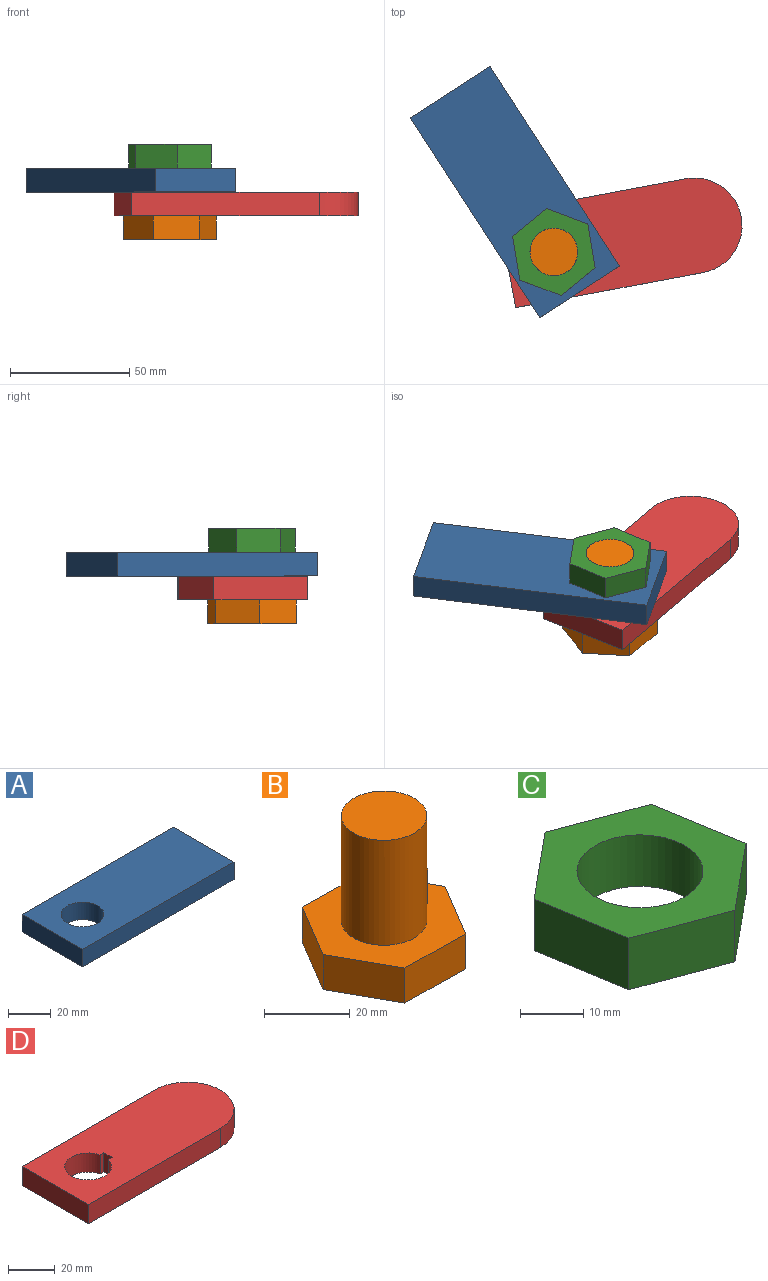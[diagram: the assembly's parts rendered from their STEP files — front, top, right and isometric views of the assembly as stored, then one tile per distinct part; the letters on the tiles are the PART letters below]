
ASSEMBLY  parts=4 mates=3
PART A: 7 faces, bbox 100x40x10 mm
  f0: plane 100x10mm, normal (0,-1,0), area 1000mm2, adj f1,f4,f5,f6
  f1: plane 40x10mm, normal (1,0,0), area 400mm2, adj f0,f2,f5,f6
  f2: plane 100x10mm, normal (0,1,0), area 1000mm2, adj f1,f4,f5,f6
  f3: cylinder r=10mm len=20mm, axis (0,0,-1), area 628.3mm2, adj f5,f6
  f4: plane 40x10mm, normal (-1,0,0), area 400mm2, adj f0,f2,f5,f6
  f5: plane 100x40mm, normal (0,0,1), area 3685.8mm2, adj f0,f1,f2,f3,f4
  f6: plane 100x40mm, normal (0,0,-1), area 3685.8mm2, adj f0,f1,f2,f3,f4
PART B: 14 faces, bbox 39.6x34.6x40 mm
  f0: cylinder r=10mm len=30mm, axis (0,0,-1), area 1834.4mm2, adj f1,f2,f3,f5,f6
  f1: plane 20x20mm, normal (0,0,1), area 314.2mm2, adj f0
  f2: plane 10x2.32mm, normal (0,1,0), area 23.2mm2, adj f0,f4,f5,f6
  f3: plane 10x2.32mm, normal (0,-1,0), area 23.2mm2, adj f0,f4,f5,f6
  f4: plane 10x5mm, normal (1,0,0), area 50mm2, adj f2,f3,f5,f6
  f5: plane 5x2.32mm, normal (0,0,1), area 10.5mm2, adj f0,f2,f3,f4
  f6: plane 39.63x34.64mm, normal (0,0,1), area 695.9mm2, adj f0,f2,f3,f4,f7,f8,f9,f10
  f7: plane 17.32x10mm, normal (-0.87,-0.49,0), area 198.2mm2, adj f6,f8,f12,f13
  f8: plane 19.82x10mm, normal (-0.02,-1,0), area 198.2mm2, adj f6,f7,f9,f13
  f9: plane 17x10.18mm, normal (0.86,-0.51,0), area 198.2mm2, adj f6,f8,f10,f13
  f10: plane 17.32x10mm, normal (0.87,0.49,0), area 198.2mm2, adj f6,f9,f11,f13
  f11: plane 19.82x10mm, normal (0.02,1,0), area 198.2mm2, adj f6,f10,f12,f13
  f12: plane 17x10.18mm, normal (-0.86,0.51,0), area 198.2mm2, adj f6,f7,f11,f13
  f13: plane 39.63x34.64mm, normal (0,0,-1), area 1020.6mm2, adj f7,f8,f9,f10,f11,f12
PART C: 9 faces, bbox 34.6x36.5x10 mm
  f0: plane 18.24x10mm, normal (-0.99,-0.17,0), area 184.9mm2, adj f1,f6,f7,f8
  f1: plane 17.32x10mm, normal (-0.35,-0.94,0), area 184.9mm2, adj f0,f2,f7,f8
  f2: plane 14.26x11.76mm, normal (0.64,-0.77,0), area 184.9mm2, adj f1,f3,f7,f8
  f3: plane 18.24x10mm, normal (0.99,0.17,0), area 184.9mm2, adj f2,f4,f7,f8
  f4: plane 17.32x10mm, normal (0.35,0.94,0), area 184.9mm2, adj f3,f6,f7,f8
  f5: cylinder r=10mm len=20mm, axis (0,0,1), area 628.3mm2, adj f7,f8
  f6: plane 14.26x11.76mm, normal (-0.64,0.77,0), area 184.9mm2, adj f0,f4,f7,f8
  f7: plane 36.47x34.64mm, normal (0,0,-1), area 574.1mm2, adj f0,f1,f2,f3,f4,f5,f6
  f8: plane 36.47x34.64mm, normal (0,0,1), area 574.1mm2, adj f0,f1,f2,f3,f4,f5,f6
PART D: 10 faces, bbox 100x40x10 mm
  f0: plane 80x10mm, normal (0,-1,0), area 800mm2, adj f1,f7,f8,f9
  f1: cylinder r=20mm len=40mm, axis (0,0,1), area 628.3mm2, adj f0,f2,f8,f9
  f2: plane 80x10mm, normal (0,1,0), area 800mm2, adj f1,f7,f8,f9
  f3: plane 10x5mm, normal (-1,0,0), area 50mm2, adj f4,f6,f8,f9
  f4: plane 10x2.32mm, normal (0,1,0), area 23.2mm2, adj f3,f5,f8,f9
  f5: cylinder r=10mm len=20mm, axis (0,0,1), area 577.8mm2, adj f4,f6,f8,f9
  f6: plane 10x2.32mm, normal (0,-1,0), area 23.2mm2, adj f3,f5,f8,f9
  f7: plane 40x10mm, normal (-1,0,0), area 400mm2, adj f0,f2,f8,f9
  f8: plane 100x40mm, normal (0,0,-1), area 3503.6mm2, adj f0,f1,f2,f3,f4,f5,f6,f7
  f9: plane 100x40mm, normal (0,0,1), area 3503.6mm2, adj f0,f1,f2,f3,f4,f5,f6,f7
PLACE A rot(axis=(0,0,1),123deg) t=(-33.23,-5.63,10.06)mm
PLACE B rot(axis=(0,0,1),10.6deg) t=(-60.89,0.26,0.06)mm
PLACE C t=(-60.89,0.26,30.06)mm
PLACE D rot(axis=(0,0,1),10.6deg) t=(-76.86,-23.08,10.06)mm
MATE revolute B.f0 <-> C.f5  axis (0,0,1) through (-60.89,0.26,30.06)mm
MATE revolute A.f3 <-> D.f5  axis (0,0,-1) through (-60.89,0.26,10.06)mm
MATE fastened B.f4 <-> D.f3  axis (0.98,0.18,0) through (-49.1,2.48,5.06)mm
